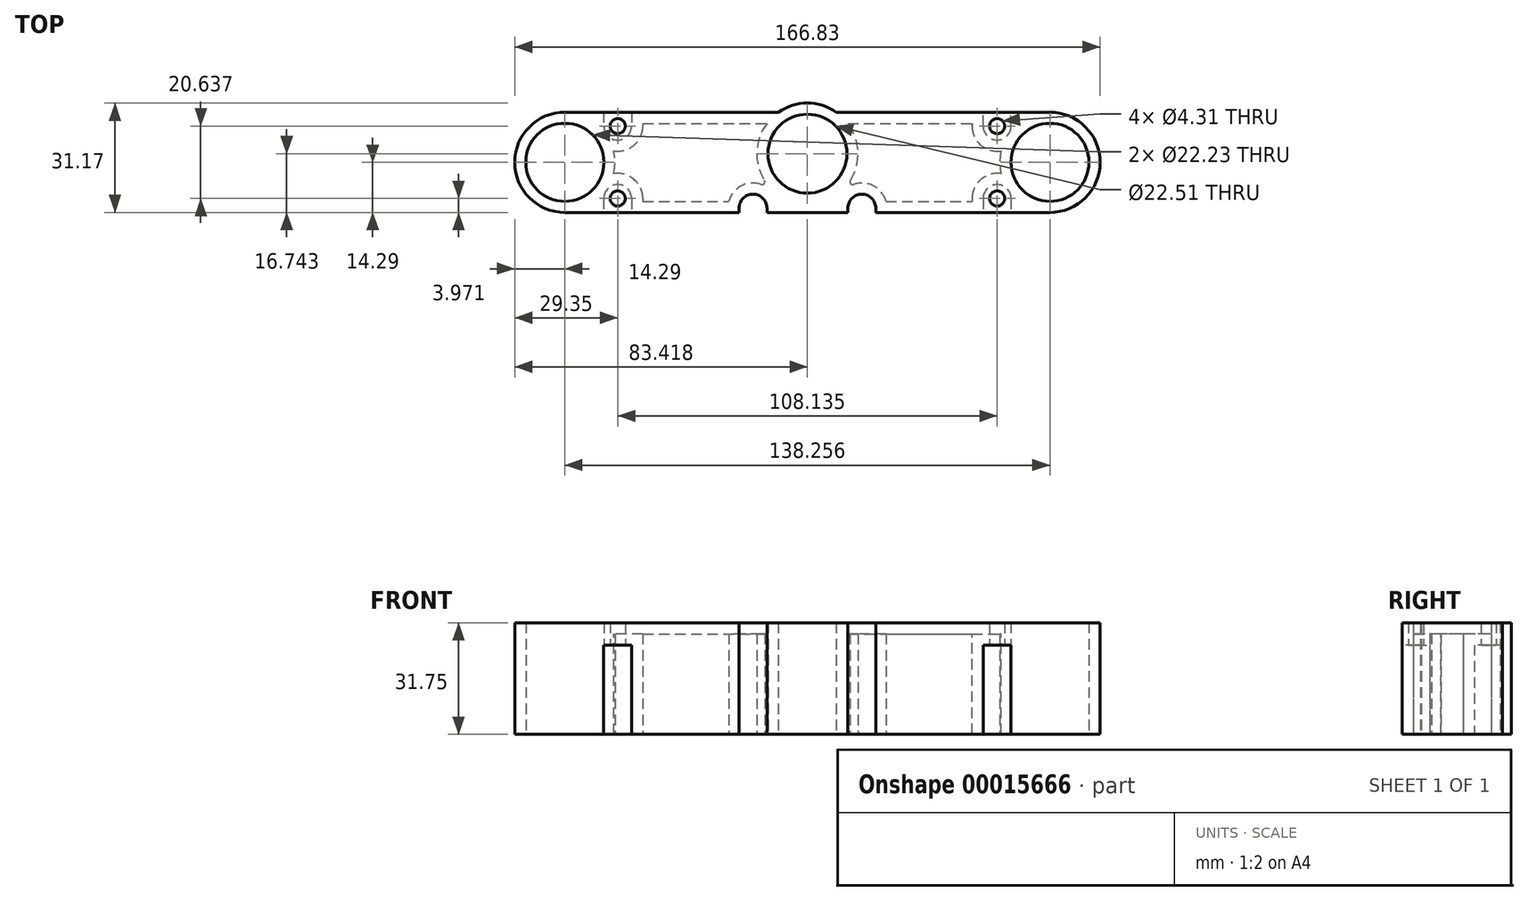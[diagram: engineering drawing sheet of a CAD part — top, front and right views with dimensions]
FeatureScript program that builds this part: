
annotation { "Feature Type Name" : "Feature", "Feature Type Description" : "" }
export const myFeature = defineFeature(function(context is Context, id is Id, definition is map)
    precondition{}
    {
        {
            var Q0;
            Q0=qCreatedBy(makeId("Top.planeOp"),FACE);
            var sketch = newSketch(context, id + "F0", { "sketchPlane" : qUnion([Q0])});
            skCircle(sketch, "E0", {"center": v(0, 0) * mm, "radius": 11.11 * mm});
            skLineSegment(sketch, "E1", {"start": v(0, 0) * mm, "end": v(-14.29, 0) * mm, "construction": true});
            skLineSegment(sketch, "E2", {"start": v(0, 0) * mm, "end": v(0, -14.29) * mm, "construction": true});
            skLineSegment(sketch, "E3.left", {"start": v(-14.29, 14.29) * mm, "end": v(-14.29, -14.29) * mm});
            skLineSegment(sketch, "E3.right", {"start": v(152.54, 14.29) * mm, "end": v(152.54, -14.29) * mm});
            skLineSegment(sketch, "E4", {"start": v(69.13, -14.29) * mm, "end": v(69.13, 2.45) * mm, "construction": true});
            skLineSegment(sketch, "E5", {"start": v(138.26, -14.29) * mm, "end": v(138.26, 0) * mm, "construction": true});
            skLineSegment(sketch, "E6", {"start": v(138.26, 0) * mm, "end": v(152.54, 0) * mm, "construction": true});
            skCircle(sketch, "E7", {"center": v(138.26, 0) * mm, "radius": 11.11 * mm});
            skLineSegment(sketch, "E8", {"start": v(0, 0) * mm, "end": v(15.06, 0) * mm, "construction": true});
            skLineSegment(sketch, "E9", {"start": v(15.06, 10.32) * mm, "end": v(15.06, -10.32) * mm, "construction": true});
            skLineSegment(sketch, "E10", {"start": v(138.26, 0) * mm, "end": v(123.2, 0) * mm, "construction": true});
            skLineSegment(sketch, "E11", {"start": v(123.2, 10.32) * mm, "end": v(123.2, -10.32) * mm, "construction": true});
            skLineSegment(sketch, "E12.bottom", {"start": v(11.1, 14.29) * mm, "end": v(19.03, 14.29) * mm, "construction": true});
            skLineSegment(sketch, "E12.top", {"start": v(11.1, 10.32) * mm, "end": v(19.03, 10.32) * mm, "construction": true});
            skLineSegment(sketch, "E12.left", {"start": v(11.1, 14.29) * mm, "end": v(11.1, 10.32) * mm});
            skLineSegment(sketch, "E12.right", {"start": v(19.03, 14.29) * mm, "end": v(19.03, 10.32) * mm});
            skLineSegment(sketch, "E13.bottom", {"start": v(11.1, -10.32) * mm, "end": v(19.03, -10.32) * mm, "construction": true});
            skLineSegment(sketch, "E13.top", {"start": v(11.1, -14.29) * mm, "end": v(19.03, -14.29) * mm, "construction": true});
            skLineSegment(sketch, "E13.left", {"start": v(11.1, -10.32) * mm, "end": v(11.1, -14.29) * mm});
            skLineSegment(sketch, "E13.right", {"start": v(19.03, -10.32) * mm, "end": v(19.03, -14.29) * mm});
            skLineSegment(sketch, "E14.bottom", {"start": v(119.23, -10.32) * mm, "end": v(127.16, -10.32) * mm, "construction": true});
            skLineSegment(sketch, "E14.top", {"start": v(119.23, -14.29) * mm, "end": v(127.16, -14.29) * mm, "construction": true});
            skLineSegment(sketch, "E14.left", {"start": v(119.23, -10.32) * mm, "end": v(119.23, -14.29) * mm});
            skLineSegment(sketch, "E14.right", {"start": v(127.16, -10.32) * mm, "end": v(127.16, -14.29) * mm});
            skLineSegment(sketch, "E15.bottom", {"start": v(127.16, 10.32) * mm, "end": v(119.23, 10.32) * mm, "construction": true});
            skLineSegment(sketch, "E15.top", {"start": v(127.16, 14.29) * mm, "end": v(119.23, 14.29) * mm, "construction": true});
            skLineSegment(sketch, "E15.left", {"start": v(127.16, 10.32) * mm, "end": v(127.16, 14.29) * mm});
            skLineSegment(sketch, "E15.right", {"start": v(119.23, 10.32) * mm, "end": v(119.23, 14.29) * mm});
            skArc(sketch, "E16", {"start": v(19.03, 10.32) * mm, "mid": v(15.06, 14.29) * mm, "end": v(11.1, 10.32) * mm, "construction": true});
            skLineSegment(sketch, "E17", {"start": v(11.1, 14.29) * mm, "end": v(-14.29, 14.29) * mm});
            skLineSegment(sketch, "E18", {"start": v(19.03, 14.29) * mm, "end": v(60.87, 14.29) * mm});
            skArc(sketch, "E19", {"start": v(11.1, 10.32) * mm, "mid": v(15.06, 6.35) * mm, "end": v(19.03, 10.32) * mm});
            skLineSegment(sketch, "E20", {"start": v(-14.29, -14.29) * mm, "end": v(11.1, -14.29) * mm});
            skLineSegment(sketch, "E21", {"start": v(127.16, -14.29) * mm, "end": v(152.54, -14.29) * mm});
            skArc(sketch, "E22", {"start": v(119.23, 10.32) * mm, "mid": v(123.2, 6.35) * mm, "end": v(127.16, 10.32) * mm});
            skArc(sketch, "E23", {"start": v(127.16, -10.32) * mm, "mid": v(123.2, -6.35) * mm, "end": v(119.23, -10.32) * mm});
            skArc(sketch, "E24", {"start": v(19.03, -10.32) * mm, "mid": v(15.06, -6.35) * mm, "end": v(11.1, -10.32) * mm});
            skLineSegment(sketch, "E25", {"start": v(77.38, 14.29) * mm, "end": v(119.23, 14.29) * mm});
            skLineSegment(sketch, "E26", {"start": v(127.16, 14.29) * mm, "end": v(152.54, 14.29) * mm});
            skCircle(sketch, "E27", {"center": v(69.13, 2.45) * mm, "radius": 11.25 * mm});
            skArc(sketch, "E28", {"start": v(77.38, 14.29) * mm, "mid": v(69.13, 16.88) * mm, "end": v(60.87, 14.29) * mm});
            skLineSegment(sketch, "E29", {"start": v(69.13, 2.45) * mm, "end": v(53.63, 2.45) * mm, "construction": true});
            skLineSegment(sketch, "E30", {"start": v(53.63, 2.45) * mm, "end": v(53.63, -13.05) * mm, "construction": true});
            skLineSegment(sketch, "E31", {"start": v(69.13, 2.45) * mm, "end": v(84.63, 2.45) * mm, "construction": true});
            skLineSegment(sketch, "E32", {"start": v(84.63, 2.45) * mm, "end": v(84.63, -13.05) * mm, "construction": true});
            skLineSegment(sketch, "E33.bottom", {"start": v(49.66, -14.29) * mm, "end": v(57.6, -14.29) * mm, "construction": true});
            skLineSegment(sketch, "E33.top", {"start": v(49.66, -13.05) * mm, "end": v(57.6, -13.05) * mm, "construction": true});
            skLineSegment(sketch, "E33.left", {"start": v(49.66, -14.29) * mm, "end": v(49.66, -13.05) * mm});
            skLineSegment(sketch, "E33.right", {"start": v(57.6, -14.29) * mm, "end": v(57.6, -13.05) * mm});
            skLineSegment(sketch, "E34.bottom", {"start": v(88.6, -14.29) * mm, "end": v(80.66, -14.29) * mm, "construction": true});
            skLineSegment(sketch, "E34.top", {"start": v(88.6, -13.05) * mm, "end": v(80.66, -13.05) * mm, "construction": true});
            skLineSegment(sketch, "E34.left", {"start": v(88.6, -14.29) * mm, "end": v(88.6, -13.05) * mm});
            skLineSegment(sketch, "E34.right", {"start": v(80.66, -14.29) * mm, "end": v(80.66, -13.05) * mm});
            skLineSegment(sketch, "E35", {"start": v(19.03, -14.29) * mm, "end": v(49.66, -14.29) * mm});
            skLineSegment(sketch, "E36", {"start": v(57.6, -14.29) * mm, "end": v(80.66, -14.29) * mm});
            skLineSegment(sketch, "E37", {"start": v(88.6, -14.29) * mm, "end": v(119.23, -14.29) * mm});
            skArc(sketch, "E38", {"start": v(57.6, -13.05) * mm, "mid": v(53.63, -9.08) * mm, "end": v(49.66, -13.05) * mm});
            skArc(sketch, "E39", {"start": v(88.6, -13.05) * mm, "mid": v(84.63, -9.08) * mm, "end": v(80.66, -13.05) * mm});
            skSolve(sketch);
        }
        {
            var Q0;
            Q0=makeQuery(id+"F0.imprint","IMPRINT",FACE,{"disambiguationData":[TD([[makeQuery(id+"F0.imprint","IMPRINT",EDGE,{"derivedFrom":sQuery(id+"F0.wireOp",EDGE,"E0")}),-1.0]])]});
            extrude(context, id + "F1", {"entities" : qUnion([Q0]), "depth" : 25.4 * mm});
        }
        {
            var Q0;
            Q0=makeQuery(id+"F1.opExtrude","CAP_FACE",FACE,{"disambiguationData":[OSD([sQuery(id+"F0.wireOp",EDGE,"E0"),sQuery(id+"F0.wireOp",EDGE,"PrSUgAgF-cG9s-TsDj-1nwa-1VO2NXHXOUih"),sQuery(id+"F0.wireOp",EDGE,"E3.left"),sQuery(id+"F0.wireOp",EDGE,"E3.right"),sQuery(id+"F0.wireOp",EDGE,"huCt0ucx-3raq-MVj7-bio3-n2narVSVME6d"),sQuery(id+"F0.wireOp",EDGE,"TAZGQied-BN7S-0w4g-mUEI-bHLIxSKkM4D3"),sQuery(id+"F0.wireOp",EDGE,"eQGrlqnH-SEcA-7PaJ-mof6-WD2IsHZTyuYQ"),sQuery(id+"F0.wireOp",EDGE,"E7"),sQuery(id+"F0.wireOp",EDGE,"7YZuQ3bp-NsQu-ZIyi-kp2P-Zave5a5pbM77"),sQuery(id+"F0.wireOp",EDGE,"E12.left"),sQuery(id+"F0.wireOp",EDGE,"E12.right"),sQuery(id+"F0.wireOp",EDGE,"E13.left"),sQuery(id+"F0.wireOp",EDGE,"E13.right"),sQuery(id+"F0.wireOp",EDGE,"E14.left"),sQuery(id+"F0.wireOp",EDGE,"E14.right"),sQuery(id+"F0.wireOp",EDGE,"E15.left"),sQuery(id+"F0.wireOp",EDGE,"E15.right"),sQuery(id+"F0.wireOp",EDGE,"E17"),sQuery(id+"F0.wireOp",EDGE,"E18"),sQuery(id+"F0.wireOp",EDGE,"E19"),sQuery(id+"F0.wireOp",EDGE,"E20"),sQuery(id+"F0.wireOp",EDGE,"YX6bz8Xi-1hWd-d6nV-AVqX-y6rGzYLUvGf4"),sQuery(id+"F0.wireOp",EDGE,"E21"),sQuery(id+"F0.wireOp",EDGE,"E22"),sQuery(id+"F0.wireOp",EDGE,"E23"),sQuery(id+"F0.wireOp",EDGE,"E24"),sQuery(id+"F0.wireOp",EDGE,"E25"),sQuery(id+"F0.wireOp",EDGE,"E26")])],"isStart":false});
            var sketch = newSketch(context, id + "F2", { "sketchPlane" : qUnion([Q0])});
            skCircle(sketch, "E40", {"center": v(15.06, -10.32) * mm, "radius": 2.15 * mm});
            skCircle(sketch, "E41", {"center": v(15.06, 10.32) * mm, "radius": 2.15 * mm});
            skCircle(sketch, "E42", {"center": v(123.2, 10.32) * mm, "radius": 2.15 * mm});
            skCircle(sketch, "E43", {"center": v(123.2, -10.32) * mm, "radius": 2.15 * mm});
            skLineSegment(sketch, "E44.bottom", {"start": v(-14.29, 14.29) * mm, "end": v(152.54, 14.29) * mm});
            skLineSegment(sketch, "E44.top", {"start": v(-14.29, -14.29) * mm, "end": v(152.54, -14.29) * mm});
            skLineSegment(sketch, "E44.left", {"start": v(-14.29, 14.29) * mm, "end": v(-14.29, -14.29) * mm, "construction": true});
            skLineSegment(sketch, "E44.right", {"start": v(152.54, 14.29) * mm, "end": v(152.54, -14.29) * mm, "construction": true});
            skSolve(sketch);
        }
        {
            var Q0;
            {var subQ24=sQuery(id+"F0.wireOp",EDGE,"E0");Q0=makeQuery(id+"F2.imprint","IMPRINT",FACE,{"disambiguationData":[TD([[makeQuery(id+"F2.imprint","IMPRINT",EDGE,{"derivedFrom":makeQuery(id+"F1.opExtrude","CAP_EDGE",EDGE,{"disambiguationData":[OSD([subQ24])],"isStart":false})}),-1.0]])]});}
            var Q1;
            Q1=makeQuery(id+"F2.imprint","IMPRINT",FACE,{"disambiguationData":[TD([[makeQuery(id+"F2.imprint","IMPRINT",EDGE,{"derivedFrom":sQuery(id+"F2.wireOp",EDGE,"E40")}),-1.0]])]});
            var Q2;
            Q2=makeQuery(id+"F2.imprint","IMPRINT",FACE,{"disambiguationData":[TD([[makeQuery(id+"F2.imprint","IMPRINT",EDGE,{"derivedFrom":sQuery(id+"F2.wireOp",EDGE,"E43")}),-1.0]])]});
            var Q3;
            Q3=makeQuery(id+"F2.imprint","IMPRINT",FACE,{"disambiguationData":[TD([[makeQuery(id+"F2.imprint","IMPRINT",EDGE,{"derivedFrom":sQuery(id+"F2.wireOp",EDGE,"E42")}),-1.0]])]});
            var Q4;
            Q4=makeQuery(id+"F2.imprint","IMPRINT",FACE,{"disambiguationData":[TD([[makeQuery(id+"F2.imprint","IMPRINT",EDGE,{"derivedFrom":sQuery(id+"F2.wireOp",EDGE,"E41")}),-1.0]])]});
            var Q5;
            {var subQ1=makeQuery(id+"F1.opExtrude","CAP_EDGE",EDGE,{"disambiguationData":[OSD([sQuery(id+"F0.wireOp",EDGE,"E28")])],"isStart":false});Q5=makeQuery(id+"F2.imprint","IMPRINT",FACE,{"disambiguationData":[TD([[makeQuery(id+"F2.imprint","IMPRINT",EDGE,{"derivedFrom":subQ1}),1.0]])]});}
            extrude(context, id + "F3", {"entities" : qUnion([Q0, Q1, Q2, Q3, Q4, Q5]), "operationType" : NewBodyOperationType.ADD, "depth" : 3.17 * mm});
        }
        {
            var Q0;
            Q0=makeQuery(id+"F3.opExtrude","CAP_FACE",FACE,{"disambiguationData":[OSD([sQuery(id+"F0.wireOp",EDGE,"E0"),sQuery(id+"F0.wireOp",EDGE,"PrSUgAgF-cG9s-TsDj-1nwa-1VO2NXHXOUih"),sQuery(id+"F0.wireOp",EDGE,"E3.left"),sQuery(id+"F0.wireOp",EDGE,"E3.right"),sQuery(id+"F0.wireOp",EDGE,"eQGrlqnH-SEcA-7PaJ-mof6-WD2IsHZTyuYQ"),sQuery(id+"F0.wireOp",EDGE,"E7"),sQuery(id+"F0.wireOp",EDGE,"7YZuQ3bp-NsQu-ZIyi-kp2P-Zave5a5pbM77"),sQuery(id+"F0.wireOp",EDGE,"E20"),sQuery(id+"F2.wireOp",EDGE,"E40"),sQuery(id+"F2.wireOp",EDGE,"E41"),sQuery(id+"F2.wireOp",EDGE,"E42"),sQuery(id+"F2.wireOp",EDGE,"E43"),sQuery(id+"F2.wireOp",EDGE,"E44.bottom"),sQuery(id+"F2.wireOp",EDGE,"E44.top")])],"isStart":false});
            var Q1;
            Q1=makeQuery(id+"F1.opExtrude","CAP_FACE",FACE,{"disambiguationData":[OSD([sQuery(id+"F0.wireOp",EDGE,"E0"),sQuery(id+"F0.wireOp",EDGE,"PrSUgAgF-cG9s-TsDj-1nwa-1VO2NXHXOUih"),sQuery(id+"F0.wireOp",EDGE,"E3.left"),sQuery(id+"F0.wireOp",EDGE,"E3.right"),sQuery(id+"F0.wireOp",EDGE,"E7"),sQuery(id+"F0.wireOp",EDGE,"7YZuQ3bp-NsQu-ZIyi-kp2P-Zave5a5pbM77"),sQuery(id+"F0.wireOp",EDGE,"E12.left"),sQuery(id+"F0.wireOp",EDGE,"E12.right"),sQuery(id+"F0.wireOp",EDGE,"E13.left"),sQuery(id+"F0.wireOp",EDGE,"E13.right"),sQuery(id+"F0.wireOp",EDGE,"E14.left"),sQuery(id+"F0.wireOp",EDGE,"E14.right"),sQuery(id+"F0.wireOp",EDGE,"E15.left"),sQuery(id+"F0.wireOp",EDGE,"E15.right"),sQuery(id+"F0.wireOp",EDGE,"E17"),sQuery(id+"F0.wireOp",EDGE,"E18"),sQuery(id+"F0.wireOp",EDGE,"E19"),sQuery(id+"F0.wireOp",EDGE,"E20"),sQuery(id+"F0.wireOp",EDGE,"YX6bz8Xi-1hWd-d6nV-AVqX-y6rGzYLUvGf4"),sQuery(id+"F0.wireOp",EDGE,"E21"),sQuery(id+"F0.wireOp",EDGE,"E22"),sQuery(id+"F0.wireOp",EDGE,"E23"),sQuery(id+"F0.wireOp",EDGE,"E24"),sQuery(id+"F0.wireOp",EDGE,"E25"),sQuery(id+"F0.wireOp",EDGE,"E26"),sQuery(id+"F0.wireOp",EDGE,"E27"),sQuery(id+"F0.wireOp",EDGE,"E28")])],"isStart":false});
            extrude(context, id + "F4", {"entities" : qUnion([Q0, Q1]), "operationType" : NewBodyOperationType.ADD, "depth" : 3.17 * mm});
        }
        {
            var Q0;
            {var subQ0=sQuery(id+"F2.wireOp",EDGE,"E44.bottom");var subQ1=sQuery(id+"F0.wireOp",EDGE,"E3.left");Q0=makeQuery(id+"F4.boolean.opBoolean","MERGE",EDGE,{"derivedFrom":[makeQuery(id+"F3.boolean.opBoolean","MERGE",EDGE,{"derivedFrom":[makeQuery(id+"F1.opExtrude","SWEPT_EDGE",EDGE,{"disambiguationData":[OSD([subQ1,sQuery(id+"F0.wireOp",EDGE,"E17")])]}),makeQuery(id+"F3.opExtrude","SWEPT_EDGE",EDGE,{"disambiguationData":[OSD([subQ1,subQ0])]})]}),makeQuery(id+"F4.opExtrude","SWEPT_EDGE",EDGE,{"disambiguationData":[OSD([subQ1,subQ0])]})]});}
            var Q1;
            {var subQ0=sQuery(id+"F2.wireOp",EDGE,"E44.top");var subQ1=sQuery(id+"F0.wireOp",EDGE,"E3.left");Q1=makeQuery(id+"F4.boolean.opBoolean","MERGE",EDGE,{"derivedFrom":[makeQuery(id+"F3.boolean.opBoolean","MERGE",EDGE,{"derivedFrom":[makeQuery(id+"F1.opExtrude","SWEPT_EDGE",EDGE,{"disambiguationData":[OSD([subQ1,sQuery(id+"F0.wireOp",EDGE,"E20")])]}),makeQuery(id+"F3.opExtrude","SWEPT_EDGE",EDGE,{"disambiguationData":[OSD([subQ1,subQ0])]})]}),makeQuery(id+"F4.opExtrude","SWEPT_EDGE",EDGE,{"disambiguationData":[OSD([subQ1,subQ0])]})]});}
            var Q2;
            {var subQ0=sQuery(id+"F2.wireOp",EDGE,"E44.bottom");var subQ1=sQuery(id+"F0.wireOp",EDGE,"E3.right");Q2=makeQuery(id+"F4.boolean.opBoolean","MERGE",EDGE,{"derivedFrom":[makeQuery(id+"F3.boolean.opBoolean","MERGE",EDGE,{"derivedFrom":[makeQuery(id+"F1.opExtrude","SWEPT_EDGE",EDGE,{"disambiguationData":[OSD([subQ1,sQuery(id+"F0.wireOp",EDGE,"E26")])]}),makeQuery(id+"F3.opExtrude","SWEPT_EDGE",EDGE,{"disambiguationData":[OSD([subQ1,subQ0])]})]}),makeQuery(id+"F4.opExtrude","SWEPT_EDGE",EDGE,{"disambiguationData":[OSD([subQ1,subQ0])]})]});}
            var Q3;
            {var subQ0=sQuery(id+"F2.wireOp",EDGE,"E44.top");var subQ1=sQuery(id+"F0.wireOp",EDGE,"E3.right");Q3=makeQuery(id+"F4.boolean.opBoolean","MERGE",EDGE,{"derivedFrom":[makeQuery(id+"F3.boolean.opBoolean","MERGE",EDGE,{"derivedFrom":[makeQuery(id+"F1.opExtrude","SWEPT_EDGE",EDGE,{"disambiguationData":[OSD([subQ1,sQuery(id+"F0.wireOp",EDGE,"E21")])]}),makeQuery(id+"F3.opExtrude","SWEPT_EDGE",EDGE,{"disambiguationData":[OSD([subQ1,subQ0])]})]}),makeQuery(id+"F4.opExtrude","SWEPT_EDGE",EDGE,{"disambiguationData":[OSD([subQ1,subQ0])]})]});}
            fillet(context, id + "F5", {"entities" : qUnion([Q0, Q1, Q2, Q3]), "radius" : 14.29 * mm, "tangentPropagation" : true, "allowEdgeOverflow" : false});
        }
        {
            var Q0;
            Q0=makeQuery(id+"F1.opExtrude","CAP_FACE",FACE,{"disambiguationData":[OSD([sQuery(id+"F0.wireOp",EDGE,"E0"),sQuery(id+"F0.wireOp",EDGE,"E3.left"),sQuery(id+"F0.wireOp",EDGE,"E3.right"),sQuery(id+"F0.wireOp",EDGE,"E7"),sQuery(id+"F0.wireOp",EDGE,"E12.left"),sQuery(id+"F0.wireOp",EDGE,"E12.right"),sQuery(id+"F0.wireOp",EDGE,"E13.left"),sQuery(id+"F0.wireOp",EDGE,"E13.right"),sQuery(id+"F0.wireOp",EDGE,"E14.left"),sQuery(id+"F0.wireOp",EDGE,"E14.right"),sQuery(id+"F0.wireOp",EDGE,"E15.left"),sQuery(id+"F0.wireOp",EDGE,"E15.right"),sQuery(id+"F0.wireOp",EDGE,"E17"),sQuery(id+"F0.wireOp",EDGE,"E18"),sQuery(id+"F0.wireOp",EDGE,"E19"),sQuery(id+"F0.wireOp",EDGE,"E20"),sQuery(id+"F0.wireOp",EDGE,"E21"),sQuery(id+"F0.wireOp",EDGE,"E22"),sQuery(id+"F0.wireOp",EDGE,"E23"),sQuery(id+"F0.wireOp",EDGE,"E24"),sQuery(id+"F0.wireOp",EDGE,"E25"),sQuery(id+"F0.wireOp",EDGE,"E26"),sQuery(id+"F0.wireOp",EDGE,"E27"),sQuery(id+"F0.wireOp",EDGE,"E28"),sQuery(id+"F0.wireOp",EDGE,"E33.left"),sQuery(id+"F0.wireOp",EDGE,"E33.right"),sQuery(id+"F0.wireOp",EDGE,"E34.left"),sQuery(id+"F0.wireOp",EDGE,"E34.right"),sQuery(id+"F0.wireOp",EDGE,"E35"),sQuery(id+"F0.wireOp",EDGE,"E36"),sQuery(id+"F0.wireOp",EDGE,"E37"),sQuery(id+"F0.wireOp",EDGE,"E38"),sQuery(id+"F0.wireOp",EDGE,"E39")])],"isStart":true});
            shell(context, id + "F6", {"entities" : qUnion([Q0]), "thickness" : 3.17 * mm});
        }
        {
            var Q0;
            Q0=makeQuery(id+"F1.opExtrude","CAP_FACE",FACE,{"disambiguationData":[OSD([sQuery(id+"F0.wireOp",EDGE,"E0"),sQuery(id+"F0.wireOp",EDGE,"E3.left"),sQuery(id+"F0.wireOp",EDGE,"E3.right"),sQuery(id+"F0.wireOp",EDGE,"E7"),sQuery(id+"F0.wireOp",EDGE,"E12.left"),sQuery(id+"F0.wireOp",EDGE,"E12.right"),sQuery(id+"F0.wireOp",EDGE,"E13.left"),sQuery(id+"F0.wireOp",EDGE,"E13.right"),sQuery(id+"F0.wireOp",EDGE,"E14.left"),sQuery(id+"F0.wireOp",EDGE,"E14.right"),sQuery(id+"F0.wireOp",EDGE,"E15.left"),sQuery(id+"F0.wireOp",EDGE,"E15.right"),sQuery(id+"F0.wireOp",EDGE,"E17"),sQuery(id+"F0.wireOp",EDGE,"E18"),sQuery(id+"F0.wireOp",EDGE,"E19"),sQuery(id+"F0.wireOp",EDGE,"E20"),sQuery(id+"F0.wireOp",EDGE,"E21"),sQuery(id+"F0.wireOp",EDGE,"E22"),sQuery(id+"F0.wireOp",EDGE,"E23"),sQuery(id+"F0.wireOp",EDGE,"E24"),sQuery(id+"F0.wireOp",EDGE,"E25"),sQuery(id+"F0.wireOp",EDGE,"E26"),sQuery(id+"F0.wireOp",EDGE,"E27"),sQuery(id+"F0.wireOp",EDGE,"E28"),sQuery(id+"F0.wireOp",EDGE,"E33.left"),sQuery(id+"F0.wireOp",EDGE,"E33.right"),sQuery(id+"F0.wireOp",EDGE,"E34.left"),sQuery(id+"F0.wireOp",EDGE,"E34.right"),sQuery(id+"F0.wireOp",EDGE,"E35"),sQuery(id+"F0.wireOp",EDGE,"E36"),sQuery(id+"F0.wireOp",EDGE,"E37"),sQuery(id+"F0.wireOp",EDGE,"E38"),sQuery(id+"F0.wireOp",EDGE,"E39")])],"isStart":true});
            var sketch = newSketch(context, id + "F7", { "sketchPlane" : qUnion([Q0])});
            skArc(sketch, "E45", {"start": v(56.89, 5.18) * mm, "mid": v(56.83, 6.06) * mm, "end": v(55.99, 6.3) * mm});
            skArc(sketch, "E46", {"start": v(81.37, 5.18) * mm, "mid": v(69.13, 11.97) * mm, "end": v(56.89, 5.18) * mm});
            skArc(sketch, "E47", {"start": v(82.27, 6.3) * mm, "mid": v(81.42, 6.06) * mm, "end": v(81.37, 5.18) * mm});
            skArc(sketch, "E48", {"start": v(82.27, 6.3) * mm, "mid": v(69.13, 14.29) * mm, "end": v(55.99, 6.3) * mm});
            skSolve(sketch);
        }
        {
            var Q0;
            Q0 = qSketchRegion(id + "F7", true);
            var Q1;
            Q1=makeQuery(id+"F6.opShell","OFFSET_FACE",FACE,{"disambiguationData":[OSD([sQuery(id+"F0.wireOp",EDGE,"E0"),sQuery(id+"F0.wireOp",EDGE,"E3.left"),sQuery(id+"F0.wireOp",EDGE,"E3.right"),sQuery(id+"F0.wireOp",EDGE,"E7"),sQuery(id+"F0.wireOp",EDGE,"E27"),sQuery(id+"F0.wireOp",EDGE,"E28"),sQuery(id+"F0.wireOp",EDGE,"E33.left"),sQuery(id+"F0.wireOp",EDGE,"E33.right"),sQuery(id+"F0.wireOp",EDGE,"E34.left"),sQuery(id+"F0.wireOp",EDGE,"E34.right"),sQuery(id+"F0.wireOp",EDGE,"E38"),sQuery(id+"F0.wireOp",EDGE,"E39"),sQuery(id+"F2.wireOp",EDGE,"E40"),sQuery(id+"F2.wireOp",EDGE,"E41"),sQuery(id+"F2.wireOp",EDGE,"E42"),sQuery(id+"F2.wireOp",EDGE,"E43"),sQuery(id+"F2.wireOp",EDGE,"E44.bottom"),sQuery(id+"F2.wireOp",EDGE,"E44.top")]),OD(0.0)]});
            extrude(context, id + "F8", {"entities" : qUnion([Q0]), "operationType" : NewBodyOperationType.ADD, "endBound" : BoundingType.UP_TO_SURFACE, "oppositeDirection" : true, "endBoundEntityFace" : qUnion([Q1]), "depth" : 25.4 * mm});
        }
    });
